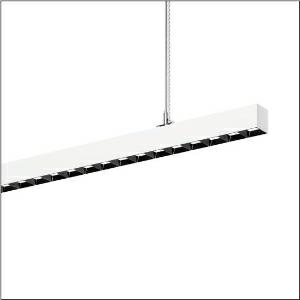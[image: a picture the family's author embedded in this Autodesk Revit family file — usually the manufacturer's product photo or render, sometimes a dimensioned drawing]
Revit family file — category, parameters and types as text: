
# Revit family: silica_r__21_51mx32dc3dwb_4ada
name_source: partatom
category: Lighting Fixtures
units: mm (PartAtom-declared; Revit-internal decimal feet)

## family parameters
Cut with Voids When Loaded = No
Host = Face
Light Source = No
Part Type = Normal
Room Calculation Point = No
Round Connector Dimension = Use Diameter
Shared = No

## types (1)
- --- (1 x LED, 18220 lm, 113 W, 3000K)
    Apparent Load = 113 VA
    CIE Flux Codes = 86 99 100 59 100
    Color Rendering = 80
    Color Temperature = 3000K
    Default Elevation = 1800 mm
    Description = Silica® 21, office luminaire, primary light control with darklight reflector, of PMMA, black, CAT 2 (L<= 3000cd/m²), light emission: direct/indirect distribution, primary light characteristic: symmetric, installation type: suspended mounting, LED, rated luminous flux: 18.220lm, luminous efficacy: 161lm/W, light colour: 830, colour temperature: 3000K, control gear: DALI 2, with terminal, 3+2-pole, max. 2.5mm², mains connection: 220..240V, AC, 50/60Hz, rated input power: 113W, luminaire housing, of aluminium, traffic white (RAL 9016), length: 3.004mm, width: 53mm, height: 53mm, protection rating (complete): IP20, insulation class (complete): insulation class I (protective earthing), certification: CE, permissible operating ambient temperature: 0..+35°C, standard: EN 50419, packaging unit: 1 piece
    Height = 53 mm
    Lamp = 1 x LED
    Lamp Light Flux = 18220 lm
    Lamp Power = 113 W
    Lamp count = 1
    Length = 3004 mm
    Luminous efficacy = 161 lm/W
    Manufacturer = Siteco
    ModVariant = No
    Model = 51MX32DC3DWB
    Mounting Place = Ceiling
    Mounting Type = Pendant
    Number of Poles = 1
    OnlyDefault = Yes
    Power Factor = 1
    Product Name = Silica® 21
    Product group = office luminaire | ceiling pendant
    ProductGroupID = 904
    Protection Class = Protection class I
    Protection Degree = IP 20
    RLX_Detail_Level = 1
    RLX_Emergency_Light_Flux = 0 lm
    RLX_Emergency_Type = 0
    RLX_Emergency_Type_DB = No
    RlxData = <blob elided: 65245 chars, md5=54dc427d>
    Socket = socket
    Standby Power = 0 W
    System Light Flux = 18220 lm
    System Power = 113 W
    Type Comments = factory setting: luminous flux: 100 % | dim-lin: 254 | 391 mA
    Type Image = l_1335871.jpg
    URL = http://relux.com
    VarID = @adj_122194
    Voltage = 0 V
    Weight = 0.00 kg
    Width = 53 mm

## geometry (parser evidence)
native form markers: Blend x4, Sweep x11
no freeform markers — native parametric forms only
